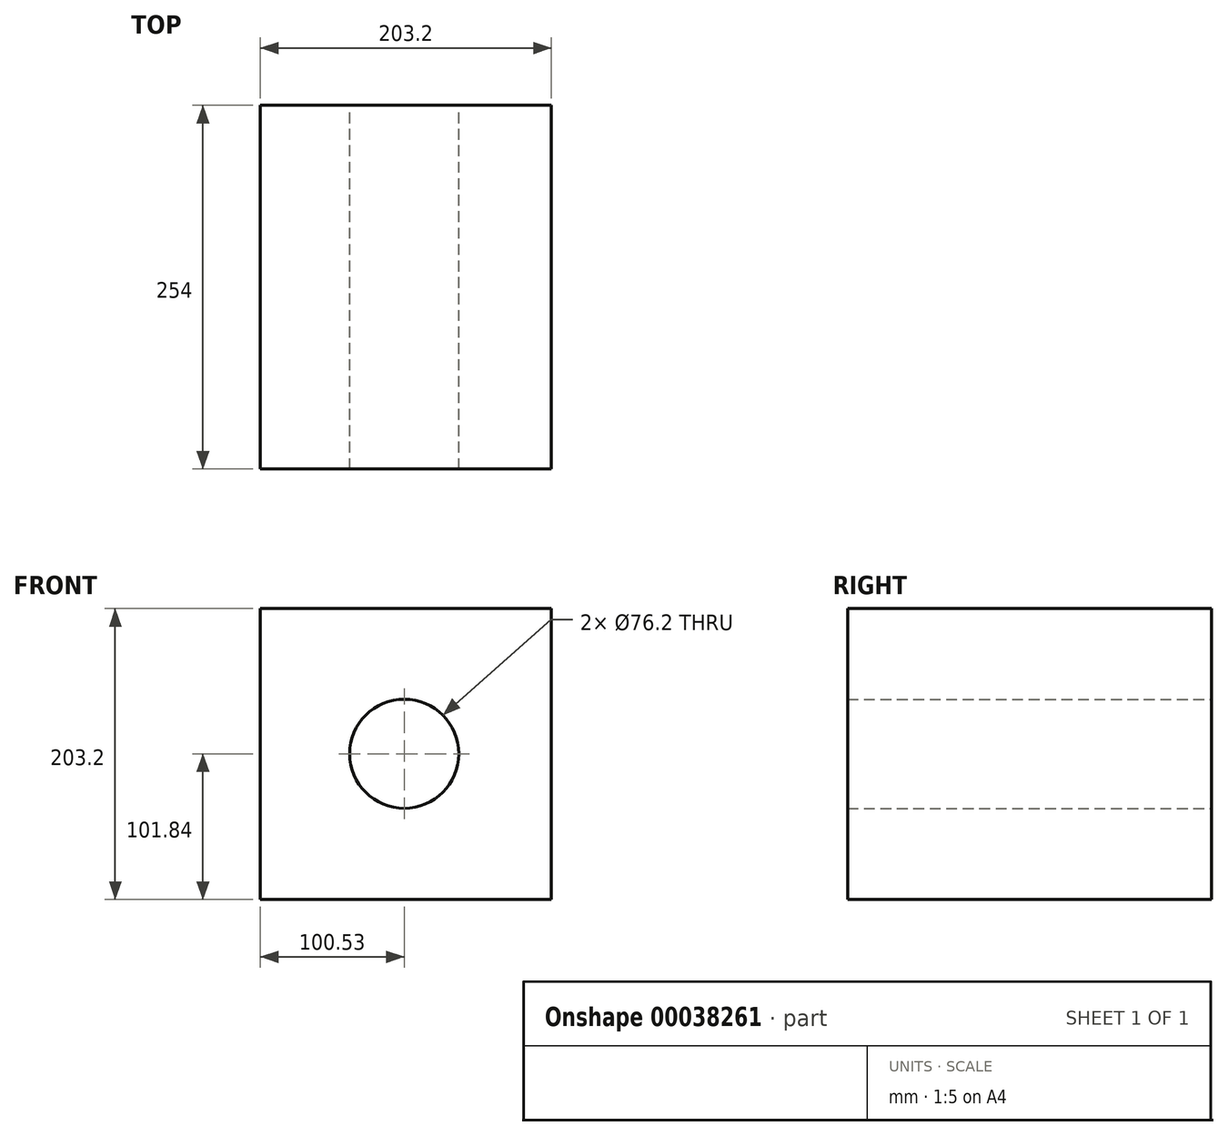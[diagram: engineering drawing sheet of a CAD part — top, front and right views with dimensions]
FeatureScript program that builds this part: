
annotation { "Feature Type Name" : "Feature", "Feature Type Description" : "" }
export const myFeature = defineFeature(function(context is Context, id is Id, definition is map)
    precondition{}
    {
        {
            var Q0;
            Q0=qCreatedBy(makeId("Front.planeOp"),FACE);
            var sketch = newSketch(context, id + "F0", { "sketchPlane" : qUnion([Q0])});
            skLineSegment(sketch, "E0.bottom", {"start": v(-100.53, -101.84) * mm, "end": v(102.67, -101.84) * mm});
            skLineSegment(sketch, "E0.top", {"start": v(-100.53, 101.36) * mm, "end": v(102.67, 101.36) * mm});
            skLineSegment(sketch, "E0.left", {"start": v(-100.53, -101.84) * mm, "end": v(-100.53, 101.36) * mm});
            skLineSegment(sketch, "E0.right", {"start": v(102.67, -101.84) * mm, "end": v(102.67, 101.36) * mm});
            skCircle(sketch, "E1", {"center": v(0, 0) * mm, "radius": 38.1 * mm});
            skSolve(sketch);
        }
        {
            var Q0;
            Q0 = qSketchRegion(id + "F0", true);
            extrude(context, id + "F1", {"entities" : qUnion([Q0]), "depth" : 254 * mm});
        }
    });
